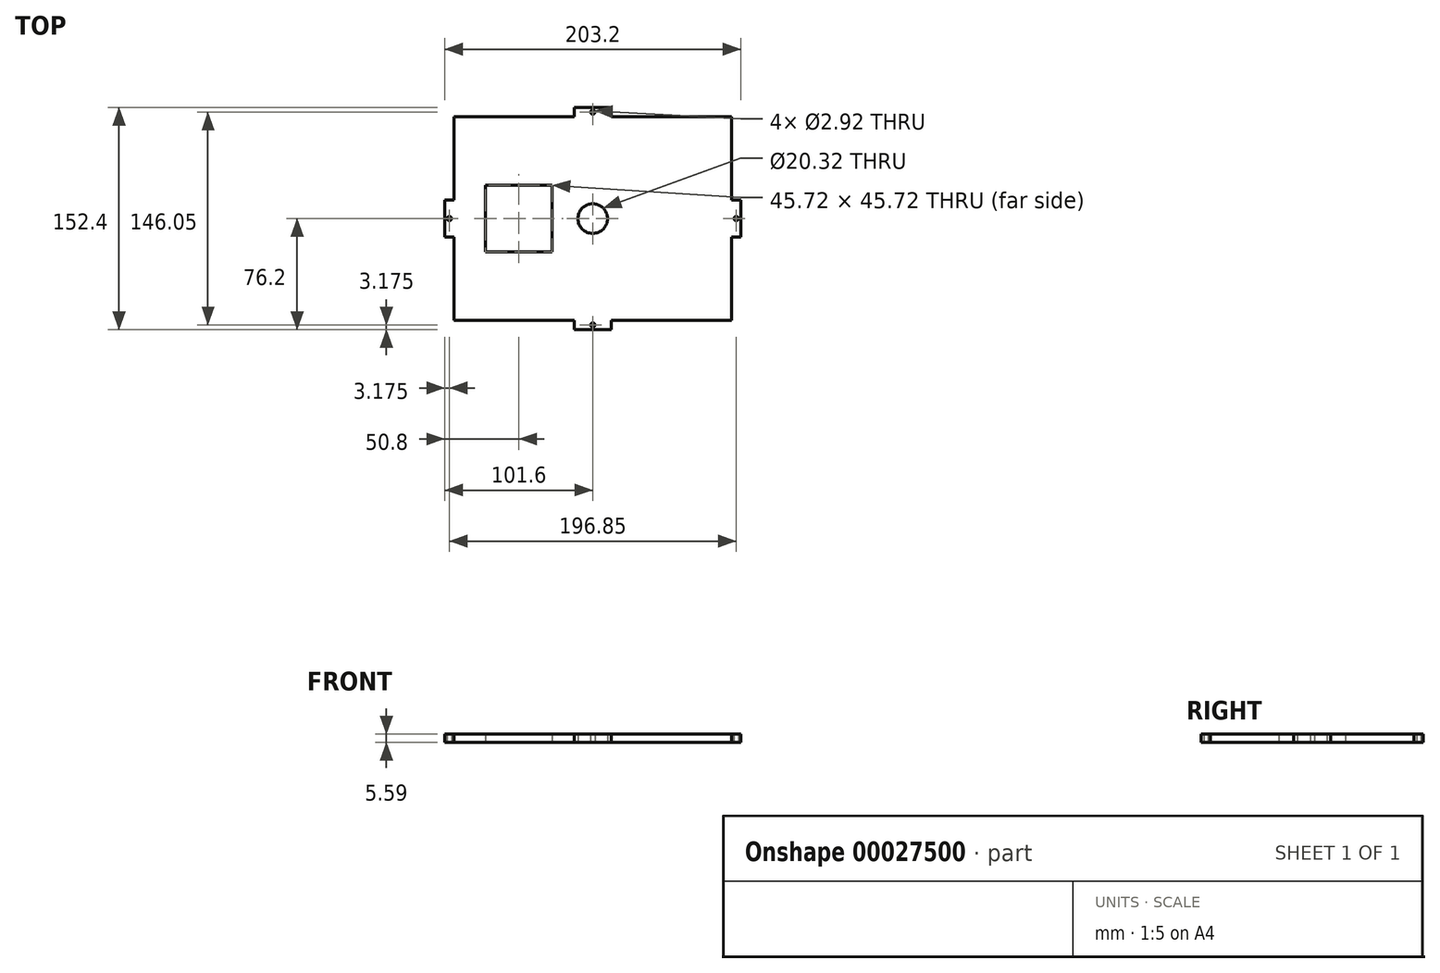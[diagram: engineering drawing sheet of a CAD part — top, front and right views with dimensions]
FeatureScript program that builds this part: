
annotation { "Feature Type Name" : "Feature", "Feature Type Description" : "" }
export const myFeature = defineFeature(function(context is Context, id is Id, definition is map)
    precondition{}
    {
        {
            var Q0;
            Q0=qCreatedBy(makeId("Top.planeOp"),FACE);
            var sketch = newSketch(context, id + "F0", { "sketchPlane" : qUnion([Q0])});
            skLineSegment(sketch, "E0.rect.bottom", {"start": v(12.7, -76.2) * mm, "end": v(-12.7, -76.2) * mm});
            skLineSegment(sketch, "E0.rect.top", {"start": v(12.7, 76.2) * mm, "end": v(-12.7, 76.2) * mm});
            skLineSegment(sketch, "E0.rect.left", {"start": v(101.6, -12.7) * mm, "end": v(101.6, 12.7) * mm});
            skLineSegment(sketch, "E0.rect.right", {"start": v(-101.6, -12.7) * mm, "end": v(-101.6, 12.7) * mm});
            skPoint(sketch, "E0.rect.middle", {"position": v(0, 0) * mm});
            skLineSegment(sketch, "E1", {"start": v(0, 76.2) * mm, "end": v(0, 69.85) * mm, "construction": true});
            skLineSegment(sketch, "E2", {"start": v(0, 0) * mm, "end": v(101.6, 0) * mm, "construction": true});
            skPoint(sketch, "E3.orphan", {"position": v(-101.6, 0) * mm});
            skLineSegment(sketch, "E4", {"start": v(0, 0) * mm, "end": v(-95.25, 0) * mm, "construction": true});
            skLineSegment(sketch, "E5", {"start": v(0, 0) * mm, "end": v(0, -76.2) * mm, "construction": true});
            skLineSegment(sketch, "E6.rect.bottom", {"start": v(-27.94, -22.86) * mm, "end": v(-73.66, -22.86) * mm});
            skLineSegment(sketch, "E6.rect.top", {"start": v(-27.94, 22.86) * mm, "end": v(-73.66, 22.86) * mm});
            skLineSegment(sketch, "E6.rect.left", {"start": v(-27.94, -22.86) * mm, "end": v(-27.94, 22.86) * mm});
            skLineSegment(sketch, "E6.rect.right", {"start": v(-73.66, -22.86) * mm, "end": v(-73.66, 22.86) * mm});
            skPoint(sketch, "E6.rect.middle", {"position": v(-50.8, 0) * mm});
            skCircle(sketch, "E7", {"center": v(0, 0) * mm, "radius": 10.16 * mm});
            skLineSegment(sketch, "E8.0", {"start": v(95.25, 69.85) * mm, "end": v(12.7, 69.85) * mm});
            skLineSegment(sketch, "E8.1", {"start": v(95.25, -69.85) * mm, "end": v(95.25, -12.7) * mm});
            skLineSegment(sketch, "E8.2", {"start": v(95.25, -69.85) * mm, "end": v(12.7, -69.85) * mm});
            skLineSegment(sketch, "E8.3", {"start": v(-95.25, -69.85) * mm, "end": v(-95.25, -12.7) * mm});
            skLineSegment(sketch, "E9.0", {"start": v(0, 12.7) * mm, "end": v(-101.6, 12.7) * mm, "construction": true});
            skLineSegment(sketch, "E10.0", {"start": v(0, -12.7) * mm, "end": v(-101.6, -12.7) * mm, "construction": true});
            skLineSegment(sketch, "E11", {"start": v(-101.6, 12.7) * mm, "end": v(-95.25, 12.7) * mm});
            skLineSegment(sketch, "E12", {"start": v(-95.25, -12.7) * mm, "end": v(-101.6, -12.7) * mm});
            skPoint(sketch, "E13.orphan", {"position": v(-101.6, -76.2) * mm});
            skPoint(sketch, "E14.orphan", {"position": v(-101.6, 76.2) * mm});
            skLineSegment(sketch, "E15.0", {"start": v(-12.7, 0) * mm, "end": v(-12.7, -76.2) * mm, "construction": true});
            skLineSegment(sketch, "E16.0", {"start": v(12.7, 0) * mm, "end": v(12.7, -76.2) * mm, "construction": true});
            skLineSegment(sketch, "E17", {"start": v(-12.7, -69.85) * mm, "end": v(-12.7, -76.2) * mm});
            skLineSegment(sketch, "E18", {"start": v(12.7, -69.85) * mm, "end": v(12.7, -76.2) * mm});
            skPoint(sketch, "E19.orphan", {"position": v(101.6, -76.2) * mm});
            skLineSegment(sketch, "E20.MirrorCS", {"start": v(101.6, 12.7) * mm, "end": v(95.25, 12.7) * mm});
            skLineSegment(sketch, "E21.MirrorCS", {"start": v(95.25, -12.7) * mm, "end": v(101.6, -12.7) * mm});
            skLineSegment(sketch, "E22.MirrorCS", {"start": v(12.7, 69.85) * mm, "end": v(12.7, 76.2) * mm});
            skLineSegment(sketch, "E23.MirrorCS", {"start": v(-12.7, 69.85) * mm, "end": v(-12.7, 76.2) * mm});
            skPoint(sketch, "E24.orphan", {"position": v(101.6, 76.2) * mm});
            skLineSegment(sketch, "E25.trimOffspring", {"start": v(-12.7, -69.85) * mm, "end": v(-95.25, -69.85) * mm});
            skLineSegment(sketch, "E26.trimOffspring", {"start": v(-95.25, 12.7) * mm, "end": v(-95.25, 69.85) * mm});
            skLineSegment(sketch, "E27.trimOffspring", {"start": v(-12.7, 69.85) * mm, "end": v(-95.25, 69.85) * mm});
            skLineSegment(sketch, "E28.trimOffspring", {"start": v(95.25, 12.7) * mm, "end": v(95.25, 69.85) * mm});
            skLineSegment(sketch, "E29", {"start": v(-95.25, 12.7) * mm, "end": v(-95.25, 0) * mm, "construction": true});
            skLineSegment(sketch, "E30", {"start": v(-12.7, 69.85) * mm, "end": v(0, 69.85) * mm, "construction": true});
            skLineSegment(sketch, "E31", {"start": v(-95.25, 0) * mm, "end": v(-95.25, -12.7) * mm, "construction": true});
            skLineSegment(sketch, "E32", {"start": v(-95.25, 0) * mm, "end": v(-101.6, 0) * mm, "construction": true});
            skLineSegment(sketch, "E33", {"start": v(0, 69.85) * mm, "end": v(12.7, 69.85) * mm, "construction": true});
            skLineSegment(sketch, "E34", {"start": v(0, 69.85) * mm, "end": v(0, 0) * mm, "construction": true});
            skCircle(sketch, "E35", {"center": v(0, 73.02) * mm, "radius": 1.46 * mm});
            skCircle(sketch, "E36", {"center": v(-98.42, 0) * mm, "radius": 1.46 * mm});
            skCircle(sketch, "E37.MirrorC", {"center": v(0, -73.02) * mm, "radius": 1.46 * mm});
            skCircle(sketch, "E38.MirrorC", {"center": v(98.42, 0) * mm, "radius": 1.46 * mm});
            skSolve(sketch);
        }
        {
            var Q0;
            Q0=makeQuery(id+"F0.imprint","IMPRINT",FACE,{"disambiguationData":[TD([[makeQuery(id+"F0.imprint","IMPRINT",EDGE,{"derivedFrom":sQuery(id+"F0.wireOp",EDGE,"E0.rect.bottom")}),-1.0]])]});
            extrude(context, id + "F1", {"entities" : qUnion([Q0]), "depth" : 5.6 * mm});
        }
    });
